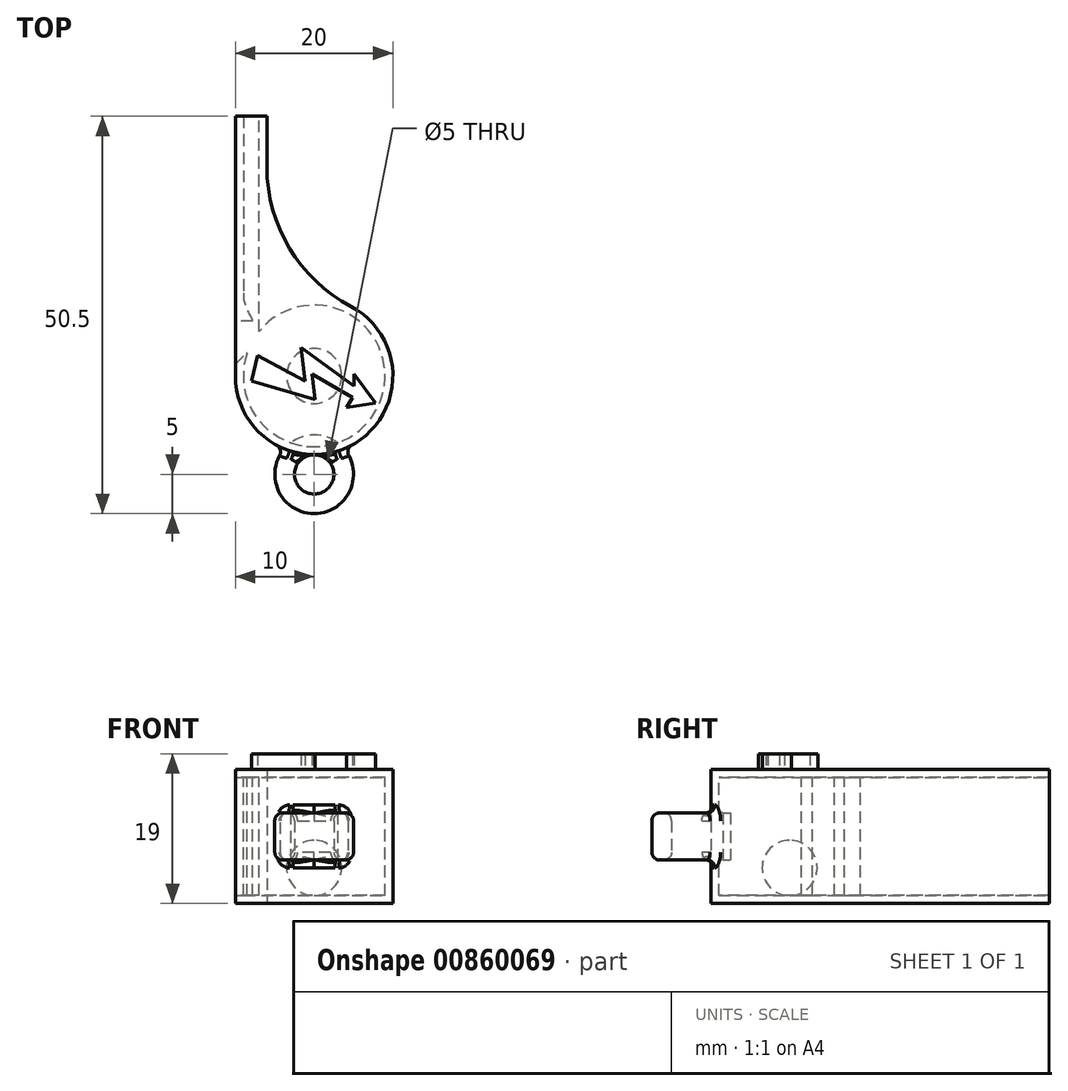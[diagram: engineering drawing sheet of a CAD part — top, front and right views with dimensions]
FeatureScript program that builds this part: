
annotation { "Feature Type Name" : "Feature", "Feature Type Description" : "" }
export const myFeature = defineFeature(function(context is Context, id is Id, definition is map)
    precondition{}
    {
        {
            var Q0;
            Q0=qCreatedBy(makeId("Top.planeOp"),FACE);
            var sketch = newSketch(context, id + "F0", { "sketchPlane" : qUnion([Q0])});
            skArc(sketch, "E0.0.4", {"start": v(-10, 0) * mm, "mid": v(5.16, -8.56) * mm, "end": v(4.67, 8.84) * mm});
            skLineSegment(sketch, "E0.0.3", {"start": v(-10, 33) * mm, "end": v(-10, 0) * mm});
            skLineSegment(sketch, "E0.0.2", {"start": v(-6, 33) * mm, "end": v(-10, 33) * mm});
            skLineSegment(sketch, "E0.0.1", {"start": v(-6, 26.53) * mm, "end": v(-6, 33) * mm});
            skArc(sketch, "E0.0.0", {"start": v(4.67, 8.84) * mm, "mid": v(-3.13, 16.2) * mm, "end": v(-6, 26.53) * mm});
            skSolve(sketch);
        }
        {
            var Q0;
            Q0=makeQuery(id+"F0.imprint","IMPRINT",FACE,{"disambiguationData":[TD([[makeQuery(id+"F0.imprint","IMPRINT",EDGE,{"derivedFrom":sQuery(id+"F0.wireOp",EDGE,"E0.0.4")}),1.0]])]});
            extrude(context, id + "F1", {"entities" : qUnion([Q0]), "endBound" : BoundingType.SYMMETRIC, "depth" : 17 * mm});
        }
        {
            var Q0;
            Q0=qCreatedBy(makeId("Top.planeOp"),FACE);
            var sketch = newSketch(context, id + "F2", { "sketchPlane" : qUnion([Q0])});
            skLineSegment(sketch, "E1.0", {"start": v(-9, 33) * mm, "end": v(-9, 10.5) * mm});
            skLineSegment(sketch, "E2.0", {"start": v(-7, 5.66) * mm, "end": v(-7, 33) * mm});
            skArc(sketch, "E3.0", {"start": v(-8.53, 2.87) * mm, "mid": v(7.89, -4.33) * mm, "end": v(-7, 5.66) * mm});
            skLineSegment(sketch, "E4.0", {"start": v(-10, 1.48) * mm, "end": v(-8.58, 2.9) * mm});
            skArc(sketch, "E5.0", {"start": v(-8.03, 7.54) * mm, "mid": v(-8.75, 8.94) * mm, "end": v(-9, 10.5) * mm});
            skArc(sketch, "E6.0", {"start": v(-7.8, 6.95) * mm, "mid": v(-7.87, 7.26) * mm, "end": v(-8.03, 7.54) * mm});
            skLineSegment(sketch, "E7.0", {"start": v(-7.8, 6.95) * mm, "end": v(-10, 6.95) * mm});
            skLineSegment(sketch, "E8", {"start": v(-7, 33) * mm, "end": v(-9, 33) * mm});
            skLineSegment(sketch, "E9", {"start": v(-10, 6.95) * mm, "end": v(-10, 1.48) * mm});
            skPoint(sketch, "E10.visualSharp", {"position": v(-8.49, 3) * mm});
            skArc(sketch, "E10.filletArc", {"start": v(-8.53, 2.87) * mm, "mid": v(-8.54, 2.9) * mm, "end": v(-8.58, 2.9) * mm});
            skSolve(sketch);
        }
        {
            var Q0;
            Q0=makeQuery(id+"F2.imprint","IMPRINT",FACE,{"disambiguationData":[TD([[makeQuery(id+"F2.imprint","IMPRINT",EDGE,{"derivedFrom":sQuery(id+"F2.wireOp",EDGE,"E1.0")}),1.0]])]});
            extrude(context, id + "F3", {"entities" : qUnion([Q0]), "operationType" : NewBodyOperationType.REMOVE, "endBound" : BoundingType.SYMMETRIC, "oppositeDirection" : true, "depth" : 15 * mm});
        }
        {
            var Q0;
            Q0=qCreatedBy(makeId("Right.planeOp"),FACE);
            var sketch = newSketch(context, id + "F4", { "sketchPlane" : qUnion([Q0])});
            skArc(sketch, "E11", {"start": v(0, -7.5) * mm, "mid": v(3.5, -4) * mm, "end": v(0, -0.5) * mm});
            skLineSegment(sketch, "E12.0", {"start": v(-9, -7.5) * mm, "end": v(9, -7.5) * mm, "construction": true});
            skLineSegment(sketch, "E13", {"start": v(0, 3.94) * mm, "end": v(0, -16.8) * mm, "construction": true});
            skLineSegment(sketch, "E14", {"start": v(0, -7.5) * mm, "end": v(0, -0.5) * mm});
            skSolve(sketch);
        }
        {
            var Q0;
            Q0=makeQuery(id+"F4.imprint","IMPRINT",FACE,{"disambiguationData":[TD([[makeQuery(id+"F4.imprint","IMPRINT",EDGE,{"derivedFrom":sQuery(id+"F4.wireOp",EDGE,"E11")}),1.0]])]});
            var Q1;
            Q1=sQuery(id+"F4.wireOp",EDGE,"E11");
            var Q2;
            Q2=sQuery(id+"F4.wireOp",EDGE,"E13");
            revolve(context, id + "F5", {"entities" : qUnion([Q0]), "surfaceEntities" : qUnion([Q1]), "axis" : qUnion([Q2]), "revolveType" : RevolveType.FULL});
        }
        {
            var Q0;
            Q0=qCreatedBy(makeId("Top.planeOp"),FACE);
            var sketch = newSketch(context, id + "F6", { "sketchPlane" : qUnion([Q0])});
            skArc(sketch, "E15", {"start": v(-3.8, -9.25) * mm, "mid": v(0, -17.5) * mm, "end": v(3.8, -9.25) * mm});
            skCircle(sketch, "E16", {"center": v(0, -12.5) * mm, "radius": 2.5 * mm});
            skPoint(sketch, "E17.orphan", {"position": v(-10, 0) * mm});
            skPoint(sketch, "E18.orphan", {"position": v(4.67, 8.84) * mm});
            skArc(sketch, "E19", {"start": v(-3.8, -9.25) * mm, "mid": v(0, -7.5) * mm, "end": v(3.8, -9.25) * mm});
            skSolve(sketch);
        }
        {
            var Q0;
            {var subQ1=sQuery(id+"F6.wireOp",EDGE,"E15");Q0=makeQuery(id+"F6.imprint","IMPRINT",FACE,{"disambiguationData":[TD([[makeQuery(id+"F6.imprint","IMPRINT",EDGE,{"derivedFrom":subQ1}),1.0]])]});}
            extrude(context, id + "F7", {"entities" : qUnion([Q0]), "operationType" : NewBodyOperationType.ADD, "endBound" : BoundingType.SYMMETRIC, "depth" : 6 * mm});
        }
        {
            var Q0;
            {var subQ0=sQuery(id+"F6.wireOp",EDGE,"E15");var subQ1=sQuery(id+"F6.wireOp",EDGE,"E19");Q0=makeQuery(id+"F7.boolean.opBoolean","SPLIT",FACE,{"disambiguationData":[TD([makeQuery(id+"F1.opExtrude","SWEPT_FACE",FACE,{"disambiguationData":[OSD([sQuery(id+"F0.wireOp",EDGE,"E0.0.4")])]})])],"derivedFrom":makeQuery(id+"F7.opExtrude","SWEPT_FACE",FACE,{"disambiguationData":[OSD([subQ0,subQ1])]})});}
            var Q1;
            {var subQ0=sQuery(id+"F6.wireOp",EDGE,"E15");var subQ1=sQuery(id+"F6.wireOp",EDGE,"E16");var subQ2=sQuery(id+"F6.wireOp",EDGE,"E19");Q1=makeQuery(id+"F7.boolean.opBoolean","SPLIT",FACE,{"disambiguationData":[TD([makeQuery(id+"F1.opExtrude","SWEPT_FACE",FACE,{"disambiguationData":[OSD([sQuery(id+"F0.wireOp",EDGE,"E0.0.4")])]})])],"derivedFrom":makeQuery(id+"F7.opExtrude","CAP_FACE",FACE,{"disambiguationData":[OSD([subQ0,subQ1,subQ2])],"isStart":false})});}
            var Q2;
            {var subQ0=sQuery(id+"F6.wireOp",EDGE,"E15");var subQ1=sQuery(id+"F6.wireOp",EDGE,"E16");var subQ2=sQuery(id+"F6.wireOp",EDGE,"E19");Q2=makeQuery(id+"F7.boolean.opBoolean","SPLIT",FACE,{"disambiguationData":[TD([makeQuery(id+"F1.opExtrude","SWEPT_FACE",FACE,{"disambiguationData":[OSD([sQuery(id+"F0.wireOp",EDGE,"E0.0.4")])]})])],"derivedFrom":makeQuery(id+"F7.opExtrude","CAP_FACE",FACE,{"disambiguationData":[OSD([subQ0,subQ1,subQ2])],"isStart":true})});}
            var Q3;
            Q3=makeQuery(id+"F3.boolean.opBoolean","COPY",EDGE,{"derivedFrom":makeQuery(id+"F3.opExtrude","CAP_EDGE",EDGE,{"disambiguationData":[OSD([sQuery(id+"F2.wireOp",EDGE,"E8")])],"isStart":true})});
            var Q4;
            Q4=makeQuery(id+"F3.boolean.opBoolean","COPY",EDGE,{"derivedFrom":makeQuery(id+"F3.opExtrude","SWEPT_EDGE",EDGE,{"disambiguationData":[OSD([sQuery(id+"F2.wireOp",EDGE,"E1.0"),sQuery(id+"F2.wireOp",EDGE,"E8")])]})});
            var Q5;
            Q5=makeQuery(id+"F3.boolean.opBoolean","COPY",EDGE,{"derivedFrom":makeQuery(id+"F3.opExtrude","SWEPT_EDGE",EDGE,{"disambiguationData":[OSD([sQuery(id+"F2.wireOp",EDGE,"E2.0"),sQuery(id+"F2.wireOp",EDGE,"E8")])]})});
            var Q6;
            Q6=makeQuery(id+"F3.boolean.opBoolean","COPY",EDGE,{"derivedFrom":makeQuery(id+"F3.opExtrude","CAP_EDGE",EDGE,{"disambiguationData":[OSD([sQuery(id+"F2.wireOp",EDGE,"E8")])],"isStart":false})});
            fillet(context, id + "F8", {"entities" : qUnion([Q0, Q1, Q2, Q3, Q4, Q5, Q6]), "radius" : 1 * mm, "tangentPropagation" : true, "allowEdgeOverflow" : false});
        }
        {
            var Q0;
            Q0=makeQuery(id+"F1.opExtrude","CAP_FACE",FACE,{"disambiguationData":[OSD([sQuery(id+"F0.wireOp",EDGE,"E0.0.4"),sQuery(id+"F0.wireOp",EDGE,"E0.0.3"),sQuery(id+"F0.wireOp",EDGE,"E0.0.2"),sQuery(id+"F0.wireOp",EDGE,"E0.0.1"),sQuery(id+"F0.wireOp",EDGE,"E0.0.0")])],"isStart":false});
            var sketch = newSketch(context, id + "F9", { "sketchPlane" : qUnion([Q0])});
            skLineSegment(sketch, "E20", {"start": v(-7.98, -0.64) * mm, "end": v(-7.2, 2.59) * mm});
            skLineSegment(sketch, "E21", {"start": v(-7.2, 2.59) * mm, "end": v(-1.13, -0.64) * mm});
            skLineSegment(sketch, "E22", {"start": v(-1.13, -0.64) * mm, "end": v(-1.68, 3.62) * mm});
            skLineSegment(sketch, "E23", {"start": v(-1.68, 3.62) * mm, "end": v(5.04, -1.27) * mm});
            skLineSegment(sketch, "E24", {"start": v(5.04, -1.27) * mm, "end": v(5.04, 0.25) * mm});
            skLineSegment(sketch, "E25", {"start": v(5.04, 0.25) * mm, "end": v(7.8, -3.44) * mm});
            skLineSegment(sketch, "E26", {"start": v(7.8, -3.44) * mm, "end": v(4.13, -3.99) * mm});
            skLineSegment(sketch, "E27", {"start": v(4.13, -3.99) * mm, "end": v(4.86, -2.73) * mm});
            skLineSegment(sketch, "E28", {"start": v(4.86, -2.73) * mm, "end": v(-0.27, 0.24) * mm});
            skLineSegment(sketch, "E29", {"start": v(-0.27, 0.24) * mm, "end": v(0.14, -3) * mm});
            skLineSegment(sketch, "E30", {"start": v(0.14, -3) * mm, "end": v(-7.98, -0.64) * mm});
            skSolve(sketch);
        }
        {
            var Q0;
            Q0=makeQuery(id+"F9.imprint","IMPRINT",FACE,{"disambiguationData":[TD([[makeQuery(id+"F9.imprint","IMPRINT",EDGE,{"derivedFrom":sQuery(id+"F9.wireOp",EDGE,"E20")}),-1.0]])]});
            extrude(context, id + "F10", {"entities" : qUnion([Q0]), "operationType" : NewBodyOperationType.ADD, "depth" : 2 * mm, "offsetDistance" : 25 * mm});
        }
    });
